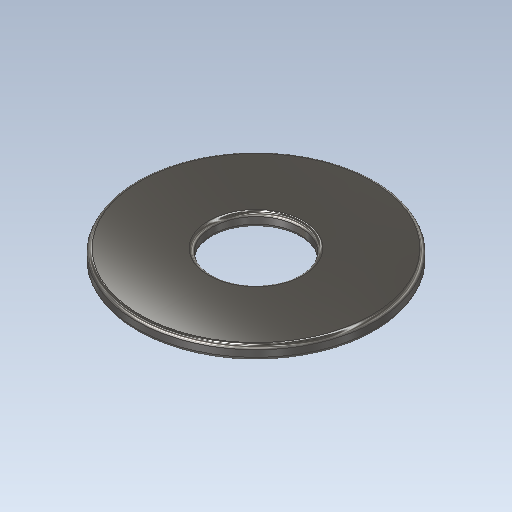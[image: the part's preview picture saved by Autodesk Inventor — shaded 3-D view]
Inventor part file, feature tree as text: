
AUTODESK INVENTOR PART (.ipt)
format: ipt  version: 2020.1 (Build 241239000, 239)  size: 143,360 bytes
history: native  units: mm
features: other x1, revolve x1, fillet x1, sketch x1
ambient origin geometry x8: Origin, YZ Plane, XZ Plane, XY Plane, X Axis, Y Axis, Z Axis, Center Point
bodies: Body1 (feature_tree)
feature tree (4):
  other  "Твердое тело1"
  revolve  "Вращение1"
  fillet  "Сопряжение3"  Radius=26.0mm
  sketch  "Эскиз1"
